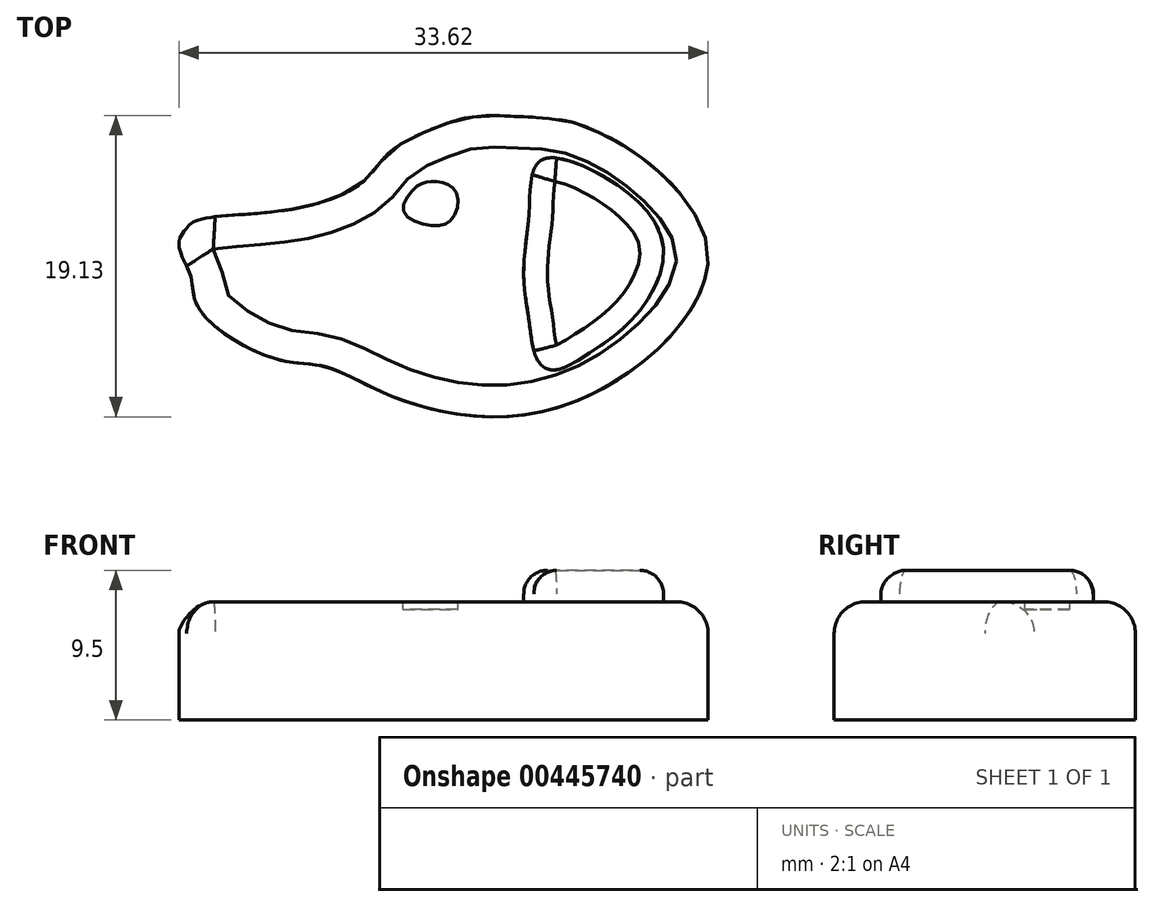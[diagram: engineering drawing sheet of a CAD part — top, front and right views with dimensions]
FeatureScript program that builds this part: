
annotation { "Feature Type Name" : "Feature", "Feature Type Description" : "" }
export const myFeature = defineFeature(function(context is Context, id is Id, definition is map)
    precondition{}
    {
        {
            var Q0;
            Q0=qCreatedBy(makeId("Top.planeOp"),FACE);
            var sketch = newSketch(context, id + "F0", { "sketchPlane" : qUnion([Q0])});
            skLineSegment(sketch, "E0.bottom", {"start": v(17.5, 15) * mm, "end": v(-17.5, 15) * mm, "construction": true});
            skLineSegment(sketch, "E0.top", {"start": v(17.5, -15) * mm, "end": v(-17.5, -15) * mm, "construction": true});
            skLineSegment(sketch, "E0.left", {"start": v(17.5, 15) * mm, "end": v(17.5, -15) * mm, "construction": true});
            skLineSegment(sketch, "E0.right", {"start": v(-17.5, 15) * mm, "end": v(-17.5, -15) * mm, "construction": true});
            skPoint(sketch, "E0.middle", {"position": v(0, 0) * mm});
            skFitSpline(sketch, "E1", {"points": [v(-3.33, -3.34) * mm, v(7.65, -3.9) * mm, v(16.73, 5.59) * mm, v(12.01, 12.17) * mm, v(9.95, 13.34) * mm, v(7.93, 14.1) * mm, v(4.74, 14.43) * mm, v(1.63, 14.39) * mm, v(-1.03, 13.54) * mm, v(-3.5, 12.17) * mm, v(-5.15, 10.31) * mm, v(-8.9, 8.7) * mm, v(-13.39, 8.17) * mm, v(-15.81, 7.8) * mm, v(-16.38, 7.36) * mm, v(-16.86, 6.56) * mm, v(-16.62, 5.43) * mm, v(-16.1, 4.17) * mm, v(-15.73, 2.44) * mm, v(-12.94, 0) * mm, v(-9.87, -1.16) * mm, v(-7.5, -1.48) * mm, v(-3.33, -3.34) * mm]});
            skFitSpline(sketch, "E2", {"points": [v(-2.6, 8.42) * mm, v(-1.86, 9.91) * mm, v(-1.05, 10.29) * mm, v(-0.14, 10.25) * mm, v(0.78, 9.54) * mm, v(0.47, 7.9) * mm, v(-0.83, 7.51) * mm, v(-2.6, 8.42) * mm]});
            skSolve(sketch);
        }
        {
            var Q0;
            Q0=makeQuery(id+"F0.imprint","IMPRINT",FACE,{"disambiguationData":[TD([[makeQuery(id+"F0.imprint","IMPRINT",EDGE,{"derivedFrom":sQuery(id+"F0.wireOp",EDGE,"E1")}),1.0]])]});
            extrude(context, id + "F1", {"entities" : qUnion([Q0]), "depth" : 7.5 * mm});
        }
        {
            var Q0;
            Q0=makeQuery(id+"F1.opExtrude","CAP_EDGE",EDGE,{"disambiguationData":[OSD([sQuery(id+"F0.wireOp",EDGE,"E1")])],"isStart":false});
            fillet(context, id + "F2", {"entities" : qUnion([Q0]), "radius" : 2 * mm, "tangentPropagation" : true, "allowEdgeOverflow" : false});
        }
        {
            var Q0;
            Q0=makeQuery(id+"F1.opExtrude","CAP_FACE",FACE,{"disambiguationData":[OSD([sQuery(id+"F0.wireOp",EDGE,"E1")])],"isStart":false});
            var sketch = newSketch(context, id + "F3", { "sketchPlane" : qUnion([Q0])});
            skFitSpline(sketch, "E3", {"points": [v(6.44, 11.78) * mm, v(5.48, 10.27) * mm, v(5.33, 7.94) * mm, v(5.02, 4.55) * mm, v(5.38, 1.31) * mm, v(5.93, -1.11) * mm, v(6.96, -1.67) * mm, v(8.96, -0.75) * mm, v(11.84, 1.48) * mm, v(13.83, 5.03) * mm, v(12.49, 8.83) * mm, v(6.44, 11.78) * mm]});
            skSolve(sketch);
        }
        {
            var Q0;
            Q0=makeQuery(id+"F3.imprint","IMPRINT",FACE,{"disambiguationData":[TD([[makeQuery(id+"F3.imprint","IMPRINT",EDGE,{"derivedFrom":sQuery(id+"F3.wireOp",EDGE,"E3")}),1.0]])]});
            extrude(context, id + "F4", {"entities" : qUnion([Q0]), "operationType" : NewBodyOperationType.ADD, "depth" : 2 * mm});
        }
        {
            var Q0;
            Q0=makeQuery(id+"F4.opExtrude","CAP_EDGE",EDGE,{"disambiguationData":[OSD([sQuery(id+"F3.wireOp",EDGE,"E3")])],"isStart":false});
            fillet(context, id + "F5", {"entities" : qUnion([Q0]), "radius" : 1.5 * mm, "tangentPropagation" : true, "allowEdgeOverflow" : false});
        }
        {
            var Q0;
            Q0=makeQuery(id+"F0.imprint","IMPRINT",FACE,{"disambiguationData":[TD([[makeQuery(id+"F0.imprint","IMPRINT",EDGE,{"derivedFrom":sQuery(id+"F0.wireOp",EDGE,"E2")}),-1.0]])]});
            extrude(context, id + "F6", {"entities" : qUnion([Q0]), "operationType" : NewBodyOperationType.ADD, "depth" : 7 * mm});
        }
    });
